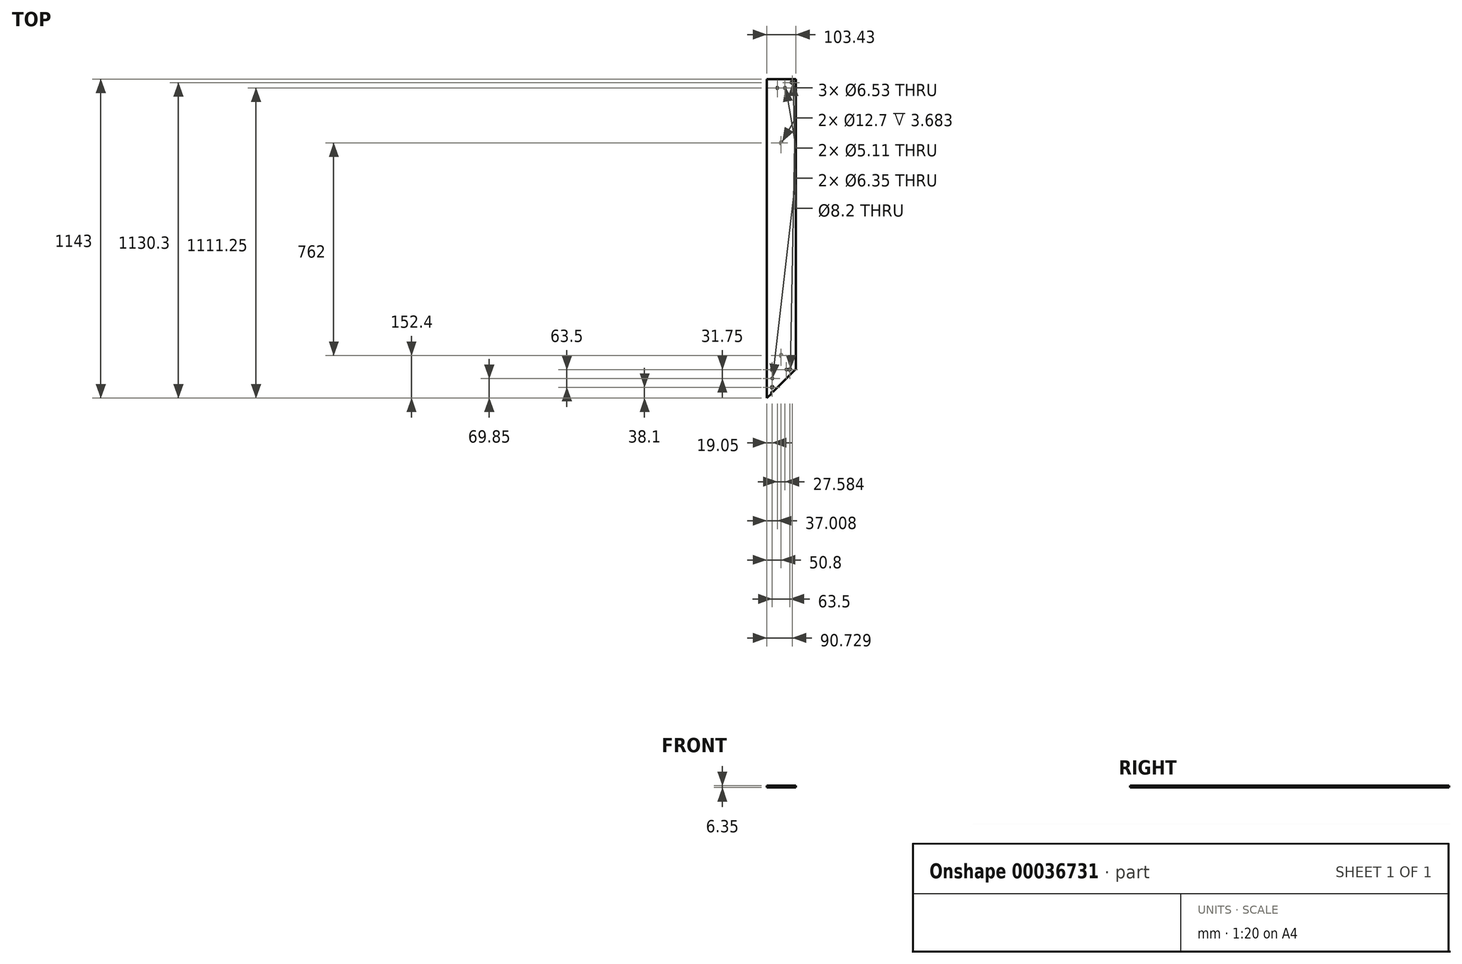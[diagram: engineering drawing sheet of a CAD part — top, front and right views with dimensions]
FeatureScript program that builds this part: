
annotation { "Feature Type Name" : "Feature", "Feature Type Description" : "" }
export const myFeature = defineFeature(function(context is Context, id is Id, definition is map)
    precondition{}
    {
        {
            var Q0;
            Q0=qCreatedBy(makeId("Top.planeOp"),FACE);
            var sketch = newSketch(context, id + "F0", { "sketchPlane" : qUnion([Q0])});
            skLineSegment(sketch, "E0", {"start": v(0, 0) * mm, "end": v(0, 1041.4) * mm});
            skLineSegment(sketch, "E1", {"start": v(0, 1041.4) * mm, "end": v(-101.6, 1041.4) * mm});
            skLineSegment(sketch, "E2", {"start": v(-101.6, 1041.4) * mm, "end": v(-101.6, -101.6) * mm});
            skLineSegment(sketch, "E3", {"start": v(0, 0) * mm, "end": v(-101.6, -101.6) * mm});
            skPoint(sketch, "E4.start.orphan", {"position": v(965.2, 0) * mm});
            skSolve(sketch);
        }
        {
            var Q0;
            Q0=makeQuery(id+"F0.imprint","IMPRINT",FACE,{"disambiguationData":[TD([[makeQuery(id+"F0.imprint","IMPRINT",EDGE,{"derivedFrom":sQuery(id+"F0.wireOp",EDGE,"E0")}),1.0]])]});
            extrude(context, id + "F1", {"entities" : qUnion([Q0]), "depth" : 6.35 * mm});
        }
        {
            var Q0;
            Q0=makeQuery(id+"F1.opExtrude","CAP_FACE",FACE,{"disambiguationData":[OSD([sQuery(id+"F0.wireOp",EDGE,"E0"),sQuery(id+"F0.wireOp",EDGE,"E1"),sQuery(id+"F0.wireOp",EDGE,"E2"),sQuery(id+"F0.wireOp",EDGE,"E3")])],"isStart":true});
            var sketch = newSketch(context, id + "F2", { "sketchPlane" : qUnion([Q0])});
            skPoint(sketch, "E5", {"position": v(-82.55, 63.5) * mm});
            skPoint(sketch, "E6", {"position": v(-19.05, 0) * mm});
            skPoint(sketch, "E7", {"position": v(-82.55, 0) * mm});
            skSolve(sketch);
        }
        {
            var Q0;
            Q0=sQuery(id+"F2.wireOp",VERTEX,"E5");
            var Q1;
            Q1=sQuery(id+"F2.wireOp",VERTEX,"E7");
            var Q2;
            Q2=sQuery(id+"F2.wireOp",VERTEX,"E6");
            var Q3;
            Q3=makeQuery(id+"F1.opExtrude","SWEPT_BODY",BODY,{"disambiguationData":[OSD([sQuery(id+"F0.wireOp",EDGE,"E0"),sQuery(id+"F0.wireOp",EDGE,"E1"),sQuery(id+"F0.wireOp",EDGE,"E2"),sQuery(id+"F0.wireOp",EDGE,"E3")])]});
            hole(context, id + "F3", {"style" : HoleStyle.C_SINK, "endStyle" : HoleEndStyle.THROUGH, "standardTappedOrClearance" : lookupTablePath({ "standard" : "ANSI", "fit" : "Close", "size" : "1/4", "type" : "Clearance" }), "standardBlindInLast" : lookupTablePath({ "fit" : "Close", "standard" : "ANSI", "size" : "1/4", "type" : "Clearance" }), "holeDiameter" : 6.53 * mm, "cSinkDiameter" : 13.5 * mm, "cSinkAngle" : 82 * degree, "tappedDepth" : 12.7 * mm, "tapClearance" : 3, "locations" : qUnion([Q0, Q1, Q2]), "scope" : qUnion([Q3])});
        }
        {
            var Q0;
            Q0=makeQuery(id+"F1.opExtrude","CAP_FACE",FACE,{"disambiguationData":[OSD([sQuery(id+"F0.wireOp",EDGE,"E0"),sQuery(id+"F0.wireOp",EDGE,"E1"),sQuery(id+"F0.wireOp",EDGE,"E2"),sQuery(id+"F0.wireOp",EDGE,"E3")])],"isStart":true});
            var sketch = newSketch(context, id + "F4", { "sketchPlane" : qUnion([Q0])});
            skCircle(sketch, "E8", {"center": v(-50.8, -50.8) * mm, "radius": 6.35 * mm});
            skCircle(sketch, "E9", {"center": v(-50.8, -812.8) * mm, "radius": 6.35 * mm});
            skSolve(sketch);
        }
        {
            var Q0;
            Q0 = qSketchRegion(id + "F4", true);
            extrude(context, id + "F5", {"entities" : qUnion([Q0]), "operationType" : NewBodyOperationType.REMOVE, "oppositeDirection" : true, "depth" : 3.68 * mm, "offsetDistance" : 25.4 * mm});
        }
        {
            var Q0;
            Q0=makeQuery(id+"F1.opExtrude","CAP_FACE",FACE,{"disambiguationData":[OSD([sQuery(id+"F0.wireOp",EDGE,"E0"),sQuery(id+"F0.wireOp",EDGE,"E1"),sQuery(id+"F0.wireOp",EDGE,"E2"),sQuery(id+"F0.wireOp",EDGE,"E3")])],"isStart":true});
            var sketch = newSketch(context, id + "F6", { "sketchPlane" : qUnion([Q0])});
            skLineSegment(sketch, "E10", {"start": v(-50.8, -1041.4) * mm, "end": v(-50.8, -909.32) * mm, "construction": true});
            skPoint(sketch, "E11", {"position": v(-37, -1009.65) * mm});
            skPoint(sketch, "E12", {"position": v(-64.6, -1009.65) * mm});
            skSolve(sketch);
        }
        {
            var Q0;
            Q0=sQuery(id+"F6.wireOp",VERTEX,"E11");
            var Q1;
            Q1=sQuery(id+"F6.wireOp",VERTEX,"E12");
            var Q2;
            Q2=makeQuery(id+"F1.opExtrude","SWEPT_BODY",BODY,{"disambiguationData":[OSD([sQuery(id+"F0.wireOp",EDGE,"E0"),sQuery(id+"F0.wireOp",EDGE,"E1"),sQuery(id+"F0.wireOp",EDGE,"E2"),sQuery(id+"F0.wireOp",EDGE,"E3")])]});
            hole(context, id + "F7", {"style" : HoleStyle.C_SINK, "endStyle" : HoleEndStyle.THROUGH, "standardTappedOrClearance" : lookupTablePath({ "standard" : "ANSI", "fit" : "Normal (ASME)", "size" : "#10", "type" : "Clearance" }), "standardBlindInLast" : lookupTablePath({ "fit" : "Free", "standard" : "ANSI", "size" : "#10", "type" : "Clearance" }), "holeDiameter" : 5.1 * mm, "cSinkDiameter" : 10.44 * mm, "cSinkAngle" : 82 * degree, "tappedDepth" : 6.35 * mm, "tapClearance" : 3, "locations" : qUnion([Q0, Q1]), "scope" : qUnion([Q2]), "majorDiameter" : 6.35 * mm});
        }
        {
            var Q0;
            Q0=makeQuery(id+"F1.opExtrude","CAP_FACE",FACE,{"disambiguationData":[OSD([sQuery(id+"F0.wireOp",EDGE,"E0"),sQuery(id+"F0.wireOp",EDGE,"E1"),sQuery(id+"F0.wireOp",EDGE,"E2"),sQuery(id+"F0.wireOp",EDGE,"E3")])],"isStart":true});
            var sketch = newSketch(context, id + "F8", { "sketchPlane" : qUnion([Q0])});
            skPoint(sketch, "E13", {"position": v(-82.55, 82.55) * mm});
            skSolve(sketch);
        }
        {
            var Q0;
            Q0=sQuery(id+"F8.wireOp",VERTEX,"E13");
            var Q1;
            Q1=makeQuery(id+"F1.opExtrude","SWEPT_BODY",BODY,{"disambiguationData":[OSD([sQuery(id+"F0.wireOp",EDGE,"E0"),sQuery(id+"F0.wireOp",EDGE,"E1"),sQuery(id+"F0.wireOp",EDGE,"E2"),sQuery(id+"F0.wireOp",EDGE,"E3")])]});
            hole(context, id + "F9", {"style" : HoleStyle.SIMPLE, "endStyle" : HoleEndStyle.THROUGH, "standardTappedOrClearance" : lookupTablePath({ "standard" : "ANSI", "fit" : "Normal (ASME)", "size" : "1/4", "type" : "Clearance" }), "standardBlindInLast" : lookupTablePath({ "fit" : "Free", "standard" : "ANSI", "size" : "1/4", "type" : "Clearance" }), "holeDiameter" : 6.76 * mm, "isTappedThrough" : true, "tappedDepth" : 6.35 * mm, "tapClearance" : 3, "locations" : qUnion([Q0]), "scope" : qUnion([Q1])});
        }
        {
            var Q0;
            Q0=makeQuery(id+"F1.opExtrude","CAP_FACE",FACE,{"disambiguationData":[OSD([sQuery(id+"F0.wireOp",EDGE,"E0"),sQuery(id+"F0.wireOp",EDGE,"E1"),sQuery(id+"F0.wireOp",EDGE,"E2"),sQuery(id+"F0.wireOp",EDGE,"E3")])],"isStart":false});
            var sketch = newSketch(context, id + "F10", { "sketchPlane" : qUnion([Q0])});
            skCircle(sketch, "E14", {"center": v(-82.55, -31.75) * mm, "radius": 3.18 * mm});
            skCircle(sketch, "E15", {"center": v(-31.75, 0) * mm, "radius": 3.18 * mm});
            skLineSegment(sketch, "E16", {"start": v(-82.55, 0) * mm, "end": v(-19.05, 0) * mm, "construction": true});
            skLineSegment(sketch, "E17", {"start": v(-82.55, 0) * mm, "end": v(-82.55, -63.5) * mm, "construction": true});
            skSolve(sketch);
        }
        {
            var Q0;
            Q0 = qSketchRegion(id + "F10", true);
            extrude(context, id + "F11", {"entities" : qUnion([Q0]), "operationType" : NewBodyOperationType.REMOVE, "endBound" : BoundingType.THROUGH_ALL, "oppositeDirection" : true, "depth" : 25.4 * mm});
        }
        {
            var Q0;
            Q0=qCreatedBy(makeId("Top.planeOp"),FACE);
            var sketch = newSketch(context, id + "F12", { "sketchPlane" : qUnion([Q0])});
            skLineSegment(sketch, "E18.bottom", {"start": v(0, 0) * mm, "end": v(1.83, 0) * mm});
            skLineSegment(sketch, "E18.top", {"start": v(0, 1041.4) * mm, "end": v(1.83, 1041.4) * mm});
            skLineSegment(sketch, "E18.left", {"start": v(0, 0) * mm, "end": v(0, 1041.4) * mm});
            skLineSegment(sketch, "E18.right", {"start": v(1.83, 0) * mm, "end": v(1.83, 1041.4) * mm});
            skSolve(sketch);
        }
        {
            var Q0;
            Q0=makeQuery(id+"F12.imprint","IMPRINT",FACE,{"disambiguationData":[TD([[makeQuery(id+"F12.imprint","IMPRINT",EDGE,{"derivedFrom":sQuery(id+"F12.wireOp",EDGE,"E18.bottom")}),1.0]])]});
            extrude(context, id + "F13", {"entities" : qUnion([Q0]), "operationType" : NewBodyOperationType.ADD, "depth" : 6.35 * mm, "offsetDistance" : 25.4 * mm});
        }
        {
            var Q0;
            Q0=makeQuery(id+"F13.boolean.opBoolean","MERGE",FACE,{"derivedFrom":[makeQuery(id+"F1.opExtrude","CAP_FACE",FACE,{"disambiguationData":[OSD([sQuery(id+"F0.wireOp",EDGE,"E0"),sQuery(id+"F0.wireOp",EDGE,"E1"),sQuery(id+"F0.wireOp",EDGE,"E2"),sQuery(id+"F0.wireOp",EDGE,"E3")])],"isStart":false}),makeQuery(id+"F13.opExtrude","CAP_FACE",FACE,{"disambiguationData":[OSD([sQuery(id+"F12.wireOp",EDGE,"E18.bottom"),sQuery(id+"F12.wireOp",EDGE,"E18.top"),sQuery(id+"F12.wireOp",EDGE,"E18.left"),sQuery(id+"F12.wireOp",EDGE,"E18.right")])],"isStart":false})]});
            var sketch = newSketch(context, id + "F14", { "sketchPlane" : qUnion([Q0])});
            skLineSegment(sketch, "E19", {"start": v(0, 0) * mm, "end": v(1.83, 1.83) * mm});
            skLineSegment(sketch, "E20", {"start": v(1.83, 1.83) * mm, "end": v(1.83, 0) * mm});
            skLineSegment(sketch, "E21", {"start": v(1.83, 0) * mm, "end": v(0, 0) * mm});
            skSolve(sketch);
        }
        {
            var Q0;
            Q0=makeQuery(id+"F14.imprint","IMPRINT",FACE,{"disambiguationData":[TD([[makeQuery(id+"F14.imprint","IMPRINT",EDGE,{"derivedFrom":sQuery(id+"F14.wireOp",EDGE,"E19")}),-1.0]])]});
            extrude(context, id + "F15", {"entities" : qUnion([Q0]), "operationType" : NewBodyOperationType.REMOVE, "oppositeDirection" : true, "depth" : 25.4 * mm, "offsetDistance" : 25.4 * mm});
        }
        {
            var Q0;
            Q0=makeQuery(id+"F13.boolean.opBoolean","MERGE",FACE,{"derivedFrom":[makeQuery(id+"F1.opExtrude","CAP_FACE",FACE,{"disambiguationData":[OSD([sQuery(id+"F0.wireOp",EDGE,"E0"),sQuery(id+"F0.wireOp",EDGE,"E1"),sQuery(id+"F0.wireOp",EDGE,"E2"),sQuery(id+"F0.wireOp",EDGE,"E3")])],"isStart":true}),makeQuery(id+"F13.opExtrude","CAP_FACE",FACE,{"disambiguationData":[OSD([sQuery(id+"F12.wireOp",EDGE,"E18.bottom"),sQuery(id+"F12.wireOp",EDGE,"E18.top"),sQuery(id+"F12.wireOp",EDGE,"E18.left"),sQuery(id+"F12.wireOp",EDGE,"E18.right")])],"isStart":true})]});
            var sketch = newSketch(context, id + "F16", { "sketchPlane" : qUnion([Q0])});
            skPoint(sketch, "E22", {"position": v(-10.87, -1028.7) * mm});
            skSolve(sketch);
        }
        {
            var Q0;
            Q0=sQuery(id+"F16.wireOp",VERTEX,"E22");
            var Q1;
            Q1=makeQuery(id+"F1.opExtrude","SWEPT_BODY",BODY,{"disambiguationData":[OSD([sQuery(id+"F0.wireOp",EDGE,"E0"),sQuery(id+"F0.wireOp",EDGE,"E1"),sQuery(id+"F0.wireOp",EDGE,"E2"),sQuery(id+"F0.wireOp",EDGE,"E3")])]});
            hole(context, id + "F17", {"style" : HoleStyle.C_SINK, "endStyle" : HoleEndStyle.THROUGH, "standardTappedOrClearance" : lookupTablePath({ "standard" : "ANSI", "fit" : "Close", "size" : "5/16", "type" : "Clearance" }), "standardBlindInLast" : lookupTablePath({ "fit" : "Close", "standard" : "ANSI", "size" : "5/16", "type" : "Clearance" }), "holeDiameter" : 8.2 * mm, "cSinkDiameter" : 16.66 * mm, "cSinkAngle" : 82 * degree, "majorDiameter" : 6.35 * mm, "tappedDepth" : 6.35 * mm, "tapClearance" : 3, "locations" : qUnion([Q0]), "scope" : qUnion([Q1])});
        }
    });
